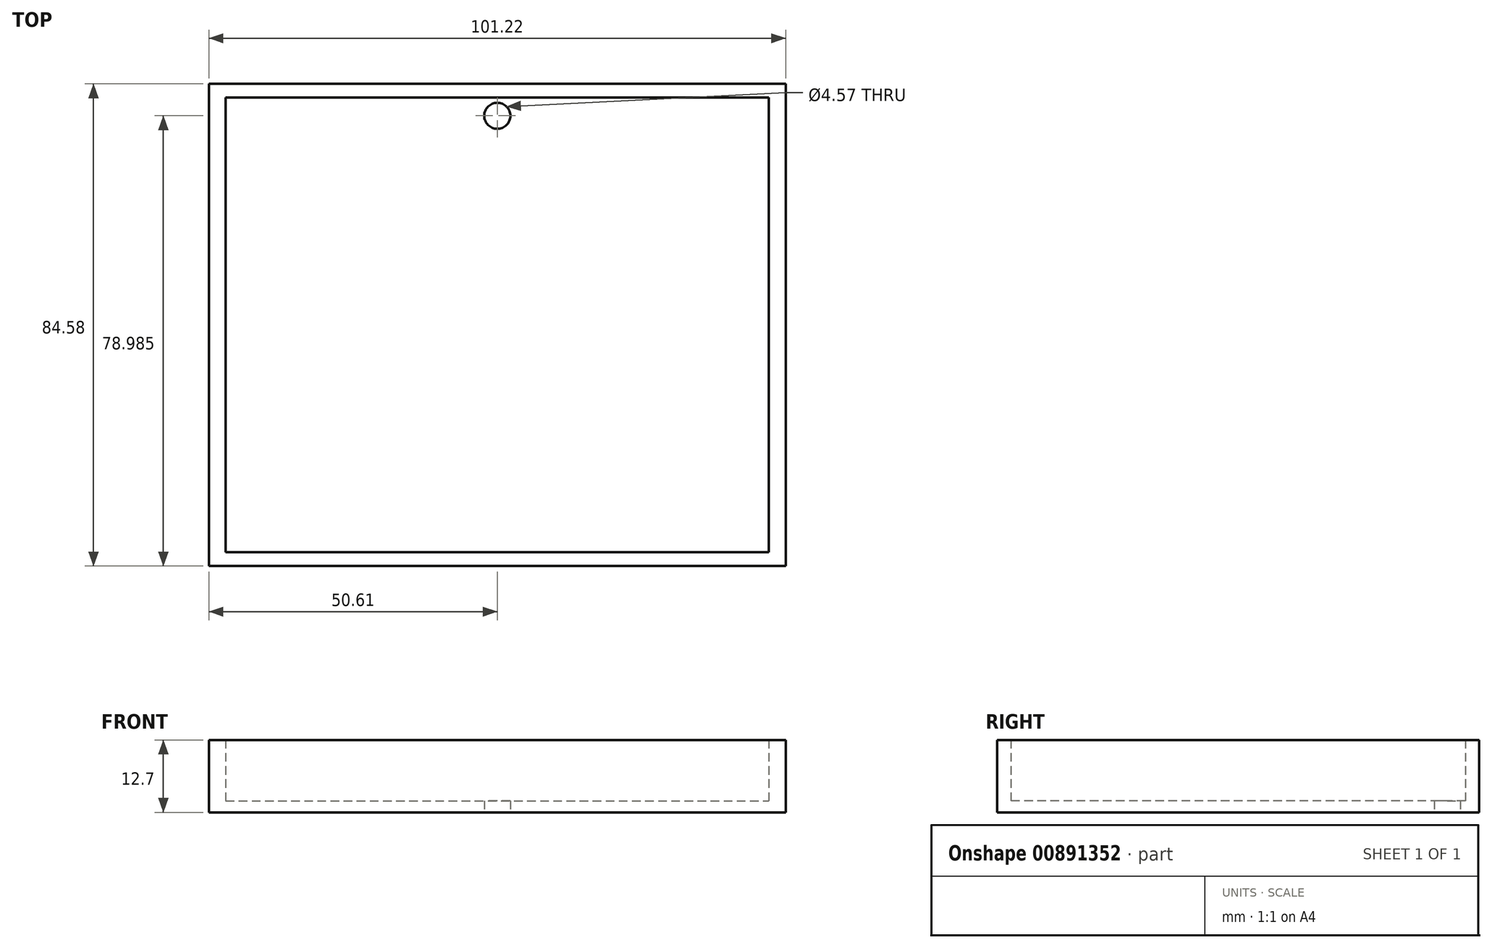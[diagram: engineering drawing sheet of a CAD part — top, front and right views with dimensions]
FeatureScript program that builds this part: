
annotation { "Feature Type Name" : "Feature", "Feature Type Description" : "" }
export const myFeature = defineFeature(function(context is Context, id is Id, definition is map)
    precondition{}
    {
        {
            var Q0;
            Q0=qCreatedBy(makeId("Top.planeOp"),FACE);
            var sketch = newSketch(context, id + "F0", { "sketchPlane" : qUnion([Q0])});
            skLineSegment(sketch, "E0.bottom", {"start": v(-47.66, 39.87) * mm, "end": v(47.66, 39.87) * mm});
            skLineSegment(sketch, "E0.top", {"start": v(-47.66, -39.87) * mm, "end": v(47.66, -39.87) * mm});
            skLineSegment(sketch, "E0.left", {"start": v(-47.66, 39.87) * mm, "end": v(-47.66, -39.87) * mm});
            skLineSegment(sketch, "E0.right", {"start": v(47.66, 39.87) * mm, "end": v(47.66, -39.87) * mm});
            skPoint(sketch, "E0.middle", {"position": v(0, 0) * mm});
            skLineSegment(sketch, "E1.bottom", {"start": v(-50.61, 42.29) * mm, "end": v(50.61, 42.29) * mm});
            skLineSegment(sketch, "E1.top", {"start": v(-50.61, -42.29) * mm, "end": v(50.61, -42.29) * mm});
            skLineSegment(sketch, "E1.left", {"start": v(-50.61, 42.29) * mm, "end": v(-50.61, -42.29) * mm});
            skLineSegment(sketch, "E1.right", {"start": v(50.61, 42.29) * mm, "end": v(50.61, -42.29) * mm});
            skSolve(sketch);
        }
        {
            var Q0;
            Q0 = qSketchRegion(id + "F0", true);
            extrude(context, id + "F1", {"entities" : qUnion([Q0]), "depth" : 12.7 * mm, "offsetDistance" : 25.4 * mm});
        }
        {
            var Q0;
            Q0=qCreatedBy(makeId("Top.planeOp"),FACE);
            var sketch = newSketch(context, id + "F2", { "sketchPlane" : qUnion([Q0])});
            skLineSegment(sketch, "E2.bottom", {"start": v(-47.66, 40.14) * mm, "end": v(47.66, 40.14) * mm});
            skLineSegment(sketch, "E2.top", {"start": v(-47.66, -40.14) * mm, "end": v(47.66, -40.14) * mm});
            skLineSegment(sketch, "E2.left", {"start": v(-47.66, 40.14) * mm, "end": v(-47.66, -40.14) * mm});
            skLineSegment(sketch, "E2.right", {"start": v(47.66, 40.14) * mm, "end": v(47.66, -40.14) * mm});
            skPoint(sketch, "E2.middle", {"position": v(0, 0) * mm});
            skSolve(sketch);
        }
        {
            var Q0;
            Q0 = qSketchRegion(id + "F2", true);
            extrude(context, id + "F3", {"entities" : qUnion([Q0]), "operationType" : NewBodyOperationType.ADD, "depth" : 2.03 * mm, "offsetDistance" : 25.4 * mm});
        }
        {
            var Q0;
            Q0=makeQuery(id+"F2.imprint","IMPRINT",FACE,{"disambiguationData":[TD([[makeQuery(id+"F2.imprint","IMPRINT",EDGE,{"derivedFrom":sQuery(id+"F2.wireOp",EDGE,"E2.bottom")}),-1.0]])]});
            var sketch = newSketch(context, id + "F4", { "sketchPlane" : qUnion([Q0])});
            skPoint(sketch, "E3", {"position": v(0, 36.7) * mm});
            skSolve(sketch);
        }
        {
            var Q0;
            Q0=sQuery(id+"F4.wireOp",VERTEX,"E3");
            var Q1;
            Q1=makeQuery(id+"F1.opExtrude","SWEPT_BODY",BODY,{"disambiguationData":[OSD([sQuery(id+"F0.wireOp",EDGE,"E0.bottom"),sQuery(id+"F0.wireOp",EDGE,"E0.top"),sQuery(id+"F0.wireOp",EDGE,"E0.left"),sQuery(id+"F0.wireOp",EDGE,"E0.right"),sQuery(id+"F0.wireOp",EDGE,"E1.bottom"),sQuery(id+"F0.wireOp",EDGE,"E1.top"),sQuery(id+"F0.wireOp",EDGE,"E1.left"),sQuery(id+"F0.wireOp",EDGE,"E1.right")])]});
            hole(context, id + "F5", {"style" : HoleStyle.C_BORE, "endStyle" : HoleEndStyle.THROUGH, "oppositeDirection" : true, "holeDiameter" : 4.57 * mm, "cBoreDiameter" : 4.57 * mm, "cBoreDepth" : 4.57 * mm, "majorDiameter" : 6.35 * mm, "isTappedThrough" : true, "tappedDepth" : 12.7 * mm, "tapClearance" : 3, "locations" : qUnion([Q0]), "scope" : qUnion([Q1])});
        }
    });
